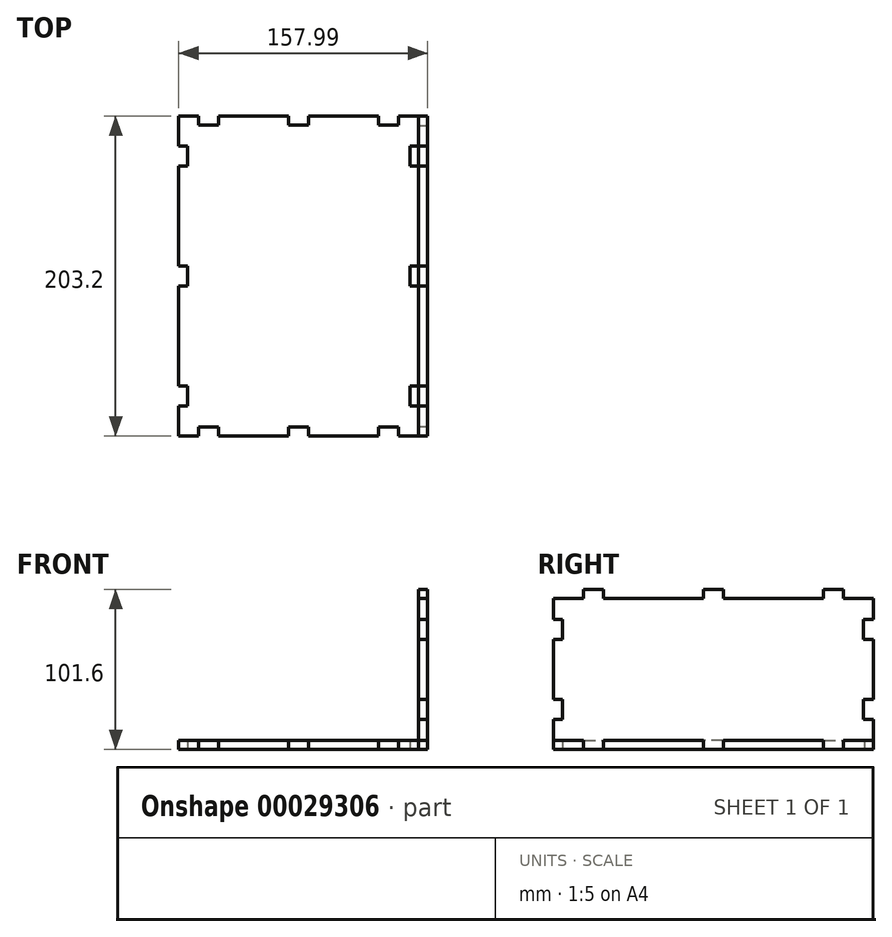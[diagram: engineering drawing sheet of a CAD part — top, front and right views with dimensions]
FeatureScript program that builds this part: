
annotation { "Feature Type Name" : "Feature", "Feature Type Description" : "" }
export const myFeature = defineFeature(function(context is Context, id is Id, definition is map)
    precondition{}
    {
        {
            var Q0;
            Q0=qCreatedBy(makeId("Top.planeOp"),FACE);
            var sketch = newSketch(context, id + "F0", { "sketchPlane" : qUnion([Q0])});
            skLineSegment(sketch, "E0", {"start": v(0, -101.6) * mm, "end": v(0, 101.6) * mm, "construction": true});
            skLineSegment(sketch, "E1", {"start": v(-76.2, 0) * mm, "end": v(76.2, 0) * mm, "construction": true});
            skLineSegment(sketch, "E2.0", {"start": v(38.1, -101.6) * mm, "end": v(38.1, 101.6) * mm, "construction": true});
            skLineSegment(sketch, "E3.0", {"start": v(76.2, -101.6) * mm, "end": v(76.2, -82.55) * mm, "construction": true});
            skLineSegment(sketch, "E4.0", {"start": v(-38.1, -101.6) * mm, "end": v(-38.1, 101.6) * mm, "construction": true});
            skLineSegment(sketch, "E5.0", {"start": v(-76.2, -101.6) * mm, "end": v(-76.2, 76.2) * mm, "construction": true});
            skLineSegment(sketch, "E6.0", {"start": v(-76.2, -50.8) * mm, "end": v(76.2, -50.8) * mm, "construction": true});
            skLineSegment(sketch, "E7.0", {"start": v(-76.2, -101.6) * mm, "end": v(-63.5, -101.6) * mm, "construction": true});
            skLineSegment(sketch, "E8.0", {"start": v(-76.2, 50.8) * mm, "end": v(76.2, 50.8) * mm, "construction": true});
            skLineSegment(sketch, "E9.0", {"start": v(-76.2, 101.6) * mm, "end": v(76.2, 101.6) * mm, "construction": true});
            skLineSegment(sketch, "E10.bottom", {"start": v(-76.2, -101.6) * mm, "end": v(-63.5, -101.6) * mm});
            skLineSegment(sketch, "E10.top", {"start": v(-76.2, 101.6) * mm, "end": v(-63.5, 101.6) * mm});
            skLineSegment(sketch, "E10.left", {"start": v(-76.2, -101.6) * mm, "end": v(-76.2, -82.55) * mm});
            skLineSegment(sketch, "E10.right", {"start": v(76.2, -101.6) * mm, "end": v(76.2, -82.55) * mm});
            skLineSegment(sketch, "E11.0", {"start": v(-57.15, -101.6) * mm, "end": v(-57.15, 101.6) * mm, "construction": true});
            skLineSegment(sketch, "E12.0", {"start": v(57.15, -101.6) * mm, "end": v(57.15, 101.6) * mm, "construction": true});
            skLineSegment(sketch, "E13.0", {"start": v(-76.2, -76.2) * mm, "end": v(76.2, -76.2) * mm, "construction": true});
            skLineSegment(sketch, "E14.0", {"start": v(-76.2, 76.2) * mm, "end": v(76.2, 76.2) * mm, "construction": true});
            skLineSegment(sketch, "E15.0", {"start": v(-76.2, -69.85) * mm, "end": v(76.2, -69.85) * mm, "construction": true});
            skLineSegment(sketch, "E16.0", {"start": v(-76.2, -82.55) * mm, "end": v(76.2, -82.55) * mm, "construction": true});
            skLineSegment(sketch, "E17.0", {"start": v(-70.61, -101.6) * mm, "end": v(-70.61, 101.6) * mm, "construction": true});
            skLineSegment(sketch, "E18.0", {"start": v(-76.2, -96.01) * mm, "end": v(76.2, -96.01) * mm, "construction": true});
            skLineSegment(sketch, "E19.0", {"start": v(-76.2, 96.01) * mm, "end": v(76.2, 96.01) * mm, "construction": true});
            skLineSegment(sketch, "E20.0", {"start": v(70.61, -101.6) * mm, "end": v(70.61, 101.6) * mm, "construction": true});
            skLineSegment(sketch, "E21", {"start": v(-76.2, -82.55) * mm, "end": v(-70.61, -82.55) * mm});
            skLineSegment(sketch, "E22", {"start": v(-70.61, -82.55) * mm, "end": v(-70.61, -69.85) * mm});
            skLineSegment(sketch, "E23", {"start": v(-70.61, -69.85) * mm, "end": v(-76.2, -69.85) * mm});
            skLineSegment(sketch, "E24", {"start": v(76.2, -82.55) * mm, "end": v(70.61, -82.55) * mm});
            skLineSegment(sketch, "E25", {"start": v(70.61, -82.55) * mm, "end": v(70.61, -69.85) * mm});
            skLineSegment(sketch, "E26", {"start": v(70.61, -69.85) * mm, "end": v(76.2, -69.85) * mm});
            skLineSegment(sketch, "E27.0", {"start": v(-76.2, 6.35) * mm, "end": v(76.2, 6.35) * mm, "construction": true});
            skLineSegment(sketch, "E28.0", {"start": v(-76.2, -6.35) * mm, "end": v(76.2, -6.35) * mm, "construction": true});
            skLineSegment(sketch, "E29", {"start": v(-76.2, -6.35) * mm, "end": v(-70.61, -6.35) * mm});
            skLineSegment(sketch, "E30.0", {"start": v(-76.2, 82.55) * mm, "end": v(76.2, 82.55) * mm, "construction": true});
            skLineSegment(sketch, "E31.0", {"start": v(-76.2, 69.85) * mm, "end": v(76.2, 69.85) * mm, "construction": true});
            skLineSegment(sketch, "E32", {"start": v(-70.61, -6.35) * mm, "end": v(-70.61, 6.35) * mm});
            skLineSegment(sketch, "E33", {"start": v(-70.61, 6.35) * mm, "end": v(-76.2, 6.35) * mm});
            skLineSegment(sketch, "E34", {"start": v(-76.2, 69.85) * mm, "end": v(-70.61, 69.85) * mm});
            skLineSegment(sketch, "E35", {"start": v(-70.61, 69.85) * mm, "end": v(-70.61, 82.55) * mm});
            skLineSegment(sketch, "E36", {"start": v(-70.61, 82.55) * mm, "end": v(-76.2, 82.55) * mm});
            skLineSegment(sketch, "E37", {"start": v(76.2, 69.85) * mm, "end": v(70.61, 69.85) * mm});
            skLineSegment(sketch, "E38", {"start": v(70.61, 69.85) * mm, "end": v(70.61, 82.55) * mm});
            skLineSegment(sketch, "E39", {"start": v(70.61, 82.55) * mm, "end": v(76.2, 82.55) * mm});
            skLineSegment(sketch, "E40", {"start": v(76.2, 6.35) * mm, "end": v(70.61, 6.35) * mm});
            skLineSegment(sketch, "E41", {"start": v(70.61, 6.35) * mm, "end": v(70.61, -6.35) * mm});
            skLineSegment(sketch, "E42", {"start": v(70.61, -6.35) * mm, "end": v(76.2, -6.35) * mm});
            skLineSegment(sketch, "E43.0", {"start": v(-63.5, -101.6) * mm, "end": v(-63.5, 101.6) * mm, "construction": true});
            skLineSegment(sketch, "E44.0", {"start": v(-50.8, -101.6) * mm, "end": v(-50.8, 101.6) * mm, "construction": true});
            skLineSegment(sketch, "E45.0", {"start": v(-6.35, -101.6) * mm, "end": v(-6.35, 101.6) * mm, "construction": true});
            skLineSegment(sketch, "E46.0", {"start": v(6.35, -101.6) * mm, "end": v(6.35, 101.6) * mm, "construction": true});
            skLineSegment(sketch, "E47.0", {"start": v(50.8, -101.6) * mm, "end": v(50.8, 101.6) * mm, "construction": true});
            skLineSegment(sketch, "E48.0", {"start": v(63.5, -101.6) * mm, "end": v(63.5, 101.6) * mm, "construction": true});
            skLineSegment(sketch, "E49", {"start": v(-63.5, -101.6) * mm, "end": v(-63.5, -96.01) * mm});
            skLineSegment(sketch, "E50", {"start": v(-63.5, -96.01) * mm, "end": v(-50.8, -96.01) * mm});
            skLineSegment(sketch, "E51", {"start": v(-50.8, -96.01) * mm, "end": v(-50.8, -101.6) * mm});
            skLineSegment(sketch, "E52", {"start": v(-6.35, -101.6) * mm, "end": v(-6.35, -96.01) * mm});
            skLineSegment(sketch, "E53", {"start": v(-6.35, -96.01) * mm, "end": v(6.35, -96.01) * mm});
            skLineSegment(sketch, "E54", {"start": v(6.35, -96.01) * mm, "end": v(6.35, -101.6) * mm});
            skLineSegment(sketch, "E55", {"start": v(50.8, -101.6) * mm, "end": v(50.8, -96.01) * mm});
            skLineSegment(sketch, "E56", {"start": v(50.8, -96.01) * mm, "end": v(63.5, -96.01) * mm});
            skLineSegment(sketch, "E57", {"start": v(63.5, -96.01) * mm, "end": v(63.5, -101.6) * mm});
            skLineSegment(sketch, "E58.trimOffspring", {"start": v(63.5, -101.6) * mm, "end": v(76.2, -101.6) * mm});
            skLineSegment(sketch, "E59.trimOffspring", {"start": v(76.2, -69.85) * mm, "end": v(76.2, -6.35) * mm});
            skLineSegment(sketch, "E60.trimOffspring", {"start": v(76.2, -69.85) * mm, "end": v(76.2, -6.35) * mm, "construction": true});
            skLineSegment(sketch, "E61.trimOffspring", {"start": v(76.2, 6.35) * mm, "end": v(76.2, 69.85) * mm});
            skLineSegment(sketch, "E62.trimOffspring", {"start": v(76.2, 6.35) * mm, "end": v(76.2, 69.85) * mm, "construction": true});
            skLineSegment(sketch, "E63.trimOffspring", {"start": v(76.2, 82.55) * mm, "end": v(76.2, 101.6) * mm});
            skLineSegment(sketch, "E64.trimOffspring", {"start": v(76.2, 82.55) * mm, "end": v(76.2, 101.6) * mm, "construction": true});
            skLineSegment(sketch, "E65.trimOffspring", {"start": v(-76.2, 82.55) * mm, "end": v(-76.2, 101.6) * mm});
            skLineSegment(sketch, "E66.trimOffspring", {"start": v(-76.2, 82.55) * mm, "end": v(-76.2, 101.6) * mm, "construction": true});
            skLineSegment(sketch, "E67.trimOffspring", {"start": v(-76.2, 6.35) * mm, "end": v(-76.2, 69.85) * mm});
            skLineSegment(sketch, "E68.trimOffspring", {"start": v(-76.2, -69.85) * mm, "end": v(-76.2, -6.35) * mm});
            skLineSegment(sketch, "E69.trimOffspring", {"start": v(-50.8, -101.6) * mm, "end": v(-6.35, -101.6) * mm});
            skLineSegment(sketch, "E70.trimOffspring", {"start": v(-57.15, -101.6) * mm, "end": v(76.2, -101.6) * mm, "construction": true});
            skLineSegment(sketch, "E71.trimOffspring", {"start": v(6.35, -101.6) * mm, "end": v(50.8, -101.6) * mm});
            skLineSegment(sketch, "E72", {"start": v(-63.5, 101.6) * mm, "end": v(-63.5, 96.01) * mm});
            skLineSegment(sketch, "E73", {"start": v(-63.5, 96.01) * mm, "end": v(-50.8, 96.01) * mm});
            skLineSegment(sketch, "E74", {"start": v(-50.8, 96.01) * mm, "end": v(-50.8, 101.6) * mm});
            skLineSegment(sketch, "E75", {"start": v(-6.35, 101.6) * mm, "end": v(-6.35, 96.01) * mm});
            skLineSegment(sketch, "E76", {"start": v(-6.35, 96.01) * mm, "end": v(6.35, 96.01) * mm});
            skLineSegment(sketch, "E77", {"start": v(6.35, 96.01) * mm, "end": v(6.35, 101.6) * mm});
            skLineSegment(sketch, "E78", {"start": v(50.8, 101.6) * mm, "end": v(50.8, 96.01) * mm});
            skLineSegment(sketch, "E79", {"start": v(50.8, 96.01) * mm, "end": v(63.5, 96.01) * mm});
            skLineSegment(sketch, "E80", {"start": v(63.5, 96.01) * mm, "end": v(63.5, 101.6) * mm});
            skLineSegment(sketch, "E81.trimOffspring", {"start": v(63.5, 101.6) * mm, "end": v(76.2, 101.6) * mm});
            skLineSegment(sketch, "E82.trimOffspring", {"start": v(6.35, 101.6) * mm, "end": v(50.8, 101.6) * mm});
            skLineSegment(sketch, "E83.trimOffspring", {"start": v(-50.8, 101.6) * mm, "end": v(-6.35, 101.6) * mm});
            skSolve(sketch);
        }
        {
            var Q0;
            Q0=makeQuery(id+"F0.imprint","IMPRINT",FACE,{"disambiguationData":[TD([[makeQuery(id+"F0.imprint","IMPRINT",EDGE,{"derivedFrom":sQuery(id+"F0.wireOp",EDGE,"E10.bottom")}),1.0]])]});
            extrude(context, id + "F1", {"entities" : qUnion([Q0]), "depth" : 5.6 * mm});
        }
        {
            var Q0;
            Q0=qCreatedBy(makeId("Right.planeOp"),FACE);
            cPlane(context, id + "F2", {"entities" : qUnion([Q0]), "cplaneType" : CPlaneType.OFFSET, "offset" : 76.2 * mm, "width" : 152.4 * mm, "height" : 152.4 * mm});
        }
        {
            var Q0;
            Q0=qCreatedBy(id+"F2.planeOp",FACE);
            var sketch = newSketch(context, id + "F3", { "sketchPlane" : qUnion([Q0])});
            skLineSegment(sketch, "E84", {"start": v(0, 0) * mm, "end": v(0, 101.6) * mm, "construction": true});
            skLineSegment(sketch, "E85", {"start": v(0, 50.8) * mm, "end": v(-101.6, 50.8) * mm, "construction": true});
            skLineSegment(sketch, "E86", {"start": v(0, 50.8) * mm, "end": v(101.6, 50.8) * mm, "construction": true});
            skPoint(sketch, "E87.0", {"position": v(-76.2, 0) * mm});
            skPoint(sketch, "E88.0", {"position": v(76.2, 0) * mm});
            skLineSegment(sketch, "E89.0", {"start": v(0, 101.6) * mm, "end": v(-101.6, 101.6) * mm, "construction": true});
            skLineSegment(sketch, "E90.0", {"start": v(0, 101.6) * mm, "end": v(101.6, 101.6) * mm, "construction": true});
            skLineSegment(sketch, "E91.0", {"start": v(101.6, 0) * mm, "end": v(101.6, 101.6) * mm, "construction": true});
            skLineSegment(sketch, "E92.0", {"start": v(-101.6, 0) * mm, "end": v(-101.6, 101.6) * mm, "construction": true});
            skLineSegment(sketch, "E93.0", {"start": v(0, 0) * mm, "end": v(-101.6, 0) * mm, "construction": true});
            skLineSegment(sketch, "E94.0", {"start": v(0, 0) * mm, "end": v(101.6, 0) * mm, "construction": true});
            skLineSegment(sketch, "E95.0", {"start": v(0, 25.4) * mm, "end": v(101.6, 25.4) * mm, "construction": true});
            skLineSegment(sketch, "E96.0", {"start": v(0, 76.2) * mm, "end": v(101.6, 76.2) * mm, "construction": true});
            skLineSegment(sketch, "E97.0", {"start": v(0, 76.2) * mm, "end": v(-101.6, 76.2) * mm, "construction": true});
            skLineSegment(sketch, "E98.0", {"start": v(0, 25.4) * mm, "end": v(-101.6, 25.4) * mm, "construction": true});
            skLineSegment(sketch, "E99.0", {"start": v(-101.6, 5.59) * mm, "end": v(-82.55, 5.59) * mm});
            skLineSegment(sketch, "E100.0", {"start": v(-82.55, 5.59) * mm, "end": v(-82.55, 0) * mm});
            skLineSegment(sketch, "E101.0", {"start": v(-69.85, 5.59) * mm, "end": v(-69.85, 0) * mm});
            skLineSegment(sketch, "E102.0", {"start": v(-69.85, 5.59) * mm, "end": v(-6.35, 5.59) * mm});
            skLineSegment(sketch, "E103.0", {"start": v(-6.35, 5.59) * mm, "end": v(-6.35, 0) * mm});
            skLineSegment(sketch, "E104.0", {"start": v(6.35, 5.59) * mm, "end": v(6.35, 0) * mm});
            skLineSegment(sketch, "E105.0", {"start": v(6.35, 5.59) * mm, "end": v(69.85, 5.59) * mm});
            skLineSegment(sketch, "E106.0", {"start": v(69.85, 5.59) * mm, "end": v(69.85, 0) * mm});
            skLineSegment(sketch, "E107.0", {"start": v(82.55, 5.59) * mm, "end": v(82.55, 0) * mm});
            skLineSegment(sketch, "E108.0", {"start": v(82.55, 5.59) * mm, "end": v(101.6, 5.59) * mm});
            skLineSegment(sketch, "E109.MirrorCS", {"start": v(-101.6, 96.01) * mm, "end": v(-82.55, 96.01) * mm});
            skLineSegment(sketch, "E110.MirrorCS", {"start": v(-82.55, 96.01) * mm, "end": v(-82.55, 101.6) * mm});
            skLineSegment(sketch, "E111.MirrorCS", {"start": v(-69.85, 96.01) * mm, "end": v(-69.85, 101.6) * mm});
            skLineSegment(sketch, "E112.MirrorCS", {"start": v(-69.85, 96.01) * mm, "end": v(-6.35, 96.01) * mm});
            skLineSegment(sketch, "E113.MirrorCS", {"start": v(-6.35, 96.01) * mm, "end": v(-6.35, 101.6) * mm});
            skLineSegment(sketch, "E114.MirrorCS", {"start": v(6.35, 96.01) * mm, "end": v(6.35, 101.6) * mm});
            skLineSegment(sketch, "E115.MirrorCS", {"start": v(6.35, 96.01) * mm, "end": v(69.85, 96.01) * mm});
            skLineSegment(sketch, "E116.MirrorCS", {"start": v(69.85, 96.01) * mm, "end": v(69.85, 101.6) * mm});
            skLineSegment(sketch, "E117.MirrorCS", {"start": v(82.55, 96.01) * mm, "end": v(82.55, 101.6) * mm});
            skLineSegment(sketch, "E118.MirrorCS", {"start": v(82.55, 96.01) * mm, "end": v(101.6, 96.01) * mm});
            skLineSegment(sketch, "E119", {"start": v(-76.2, 0) * mm, "end": v(-76.2, 101.6) * mm, "construction": true});
            skLineSegment(sketch, "E120", {"start": v(76.2, 0) * mm, "end": v(76.2, 101.6) * mm, "construction": true});
            skLineSegment(sketch, "E121", {"start": v(-82.55, 101.6) * mm, "end": v(-69.85, 101.6) * mm});
            skLineSegment(sketch, "E122", {"start": v(-6.35, 101.6) * mm, "end": v(6.35, 101.6) * mm});
            skLineSegment(sketch, "E123", {"start": v(69.85, 101.6) * mm, "end": v(82.55, 101.6) * mm});
            skLineSegment(sketch, "E124.0", {"start": v(0, 31.75) * mm, "end": v(-101.6, 31.75) * mm, "construction": true});
            skLineSegment(sketch, "E125.0", {"start": v(0, 19.05) * mm, "end": v(-101.6, 19.05) * mm, "construction": true});
            skLineSegment(sketch, "E126.0", {"start": v(-96.01, 0) * mm, "end": v(-96.01, 101.6) * mm, "construction": true});
            skLineSegment(sketch, "E127.0", {"start": v(95.25, 0) * mm, "end": v(95.25, 101.6) * mm, "construction": true});
            skLineSegment(sketch, "E128.0", {"start": v(0, 69.85) * mm, "end": v(-101.6, 69.85) * mm, "construction": true});
            skLineSegment(sketch, "E129.0", {"start": v(0, 82.55) * mm, "end": v(-101.6, 82.55) * mm, "construction": true});
            skLineSegment(sketch, "E130.0", {"start": v(0, 82.55) * mm, "end": v(101.6, 82.55) * mm, "construction": true});
            skLineSegment(sketch, "E131.0", {"start": v(0, 69.85) * mm, "end": v(101.6, 69.85) * mm, "construction": true});
            skLineSegment(sketch, "E132.0", {"start": v(0, 19.05) * mm, "end": v(101.6, 19.05) * mm, "construction": true});
            skLineSegment(sketch, "E133.0", {"start": v(0, 31.75) * mm, "end": v(101.6, 31.75) * mm, "construction": true});
            skLineSegment(sketch, "E134", {"start": v(-101.6, 96.01) * mm, "end": v(-101.6, 82.55) * mm});
            skLineSegment(sketch, "E135", {"start": v(-101.6, 82.55) * mm, "end": v(-96.01, 82.55) * mm});
            skLineSegment(sketch, "E136", {"start": v(-96.01, 82.55) * mm, "end": v(-96.01, 69.85) * mm});
            skLineSegment(sketch, "E137", {"start": v(-96.01, 69.85) * mm, "end": v(-101.6, 69.85) * mm});
            skLineSegment(sketch, "E138", {"start": v(-101.6, 69.85) * mm, "end": v(-101.6, 31.75) * mm});
            skLineSegment(sketch, "E139", {"start": v(-101.6, 31.75) * mm, "end": v(-96.01, 31.75) * mm});
            skLineSegment(sketch, "E140", {"start": v(-96.01, 31.75) * mm, "end": v(-96.01, 19.05) * mm});
            skLineSegment(sketch, "E141", {"start": v(-96.01, 19.05) * mm, "end": v(-101.6, 19.05) * mm});
            skLineSegment(sketch, "E142", {"start": v(-101.6, 19.05) * mm, "end": v(-101.6, 5.59) * mm});
            skLineSegment(sketch, "E143", {"start": v(101.6, 5.59) * mm, "end": v(101.6, 19.05) * mm});
            skLineSegment(sketch, "E144", {"start": v(95.25, 19.05) * mm, "end": v(95.25, 31.75) * mm});
            skLineSegment(sketch, "E145", {"start": v(95.25, 31.75) * mm, "end": v(101.6, 31.75) * mm});
            skLineSegment(sketch, "E146", {"start": v(101.6, 31.75) * mm, "end": v(101.6, 69.85) * mm});
            skLineSegment(sketch, "E147", {"start": v(95.25, 69.85) * mm, "end": v(95.25, 82.55) * mm});
            skLineSegment(sketch, "E148", {"start": v(95.25, 82.55) * mm, "end": v(101.6, 82.55) * mm});
            skLineSegment(sketch, "E149", {"start": v(101.6, 82.55) * mm, "end": v(101.6, 96.01) * mm});
            skLineSegment(sketch, "E150", {"start": v(101.6, 69.85) * mm, "end": v(95.25, 69.85) * mm});
            skLineSegment(sketch, "E151", {"start": v(101.6, 19.05) * mm, "end": v(95.25, 19.05) * mm});
            skLineSegment(sketch, "E152", {"start": v(-82.55, 0) * mm, "end": v(-69.85, 0) * mm});
            skLineSegment(sketch, "E153", {"start": v(-6.35, 0) * mm, "end": v(6.35, 0) * mm});
            skLineSegment(sketch, "E154", {"start": v(69.85, 0) * mm, "end": v(82.55, 0) * mm});
            skSolve(sketch);
        }
        {
            var Q0;
            Q0=makeQuery(id+"F3.imprint","IMPRINT",FACE,{"disambiguationData":[TD([[makeQuery(id+"F3.imprint","IMPRINT",EDGE,{"derivedFrom":sQuery(id+"F3.wireOp",EDGE,"E99.0")}),1.0]])]});
            extrude(context, id + "F4", {"entities" : qUnion([Q0]), "depth" : 5.6 * mm});
        }
    });
